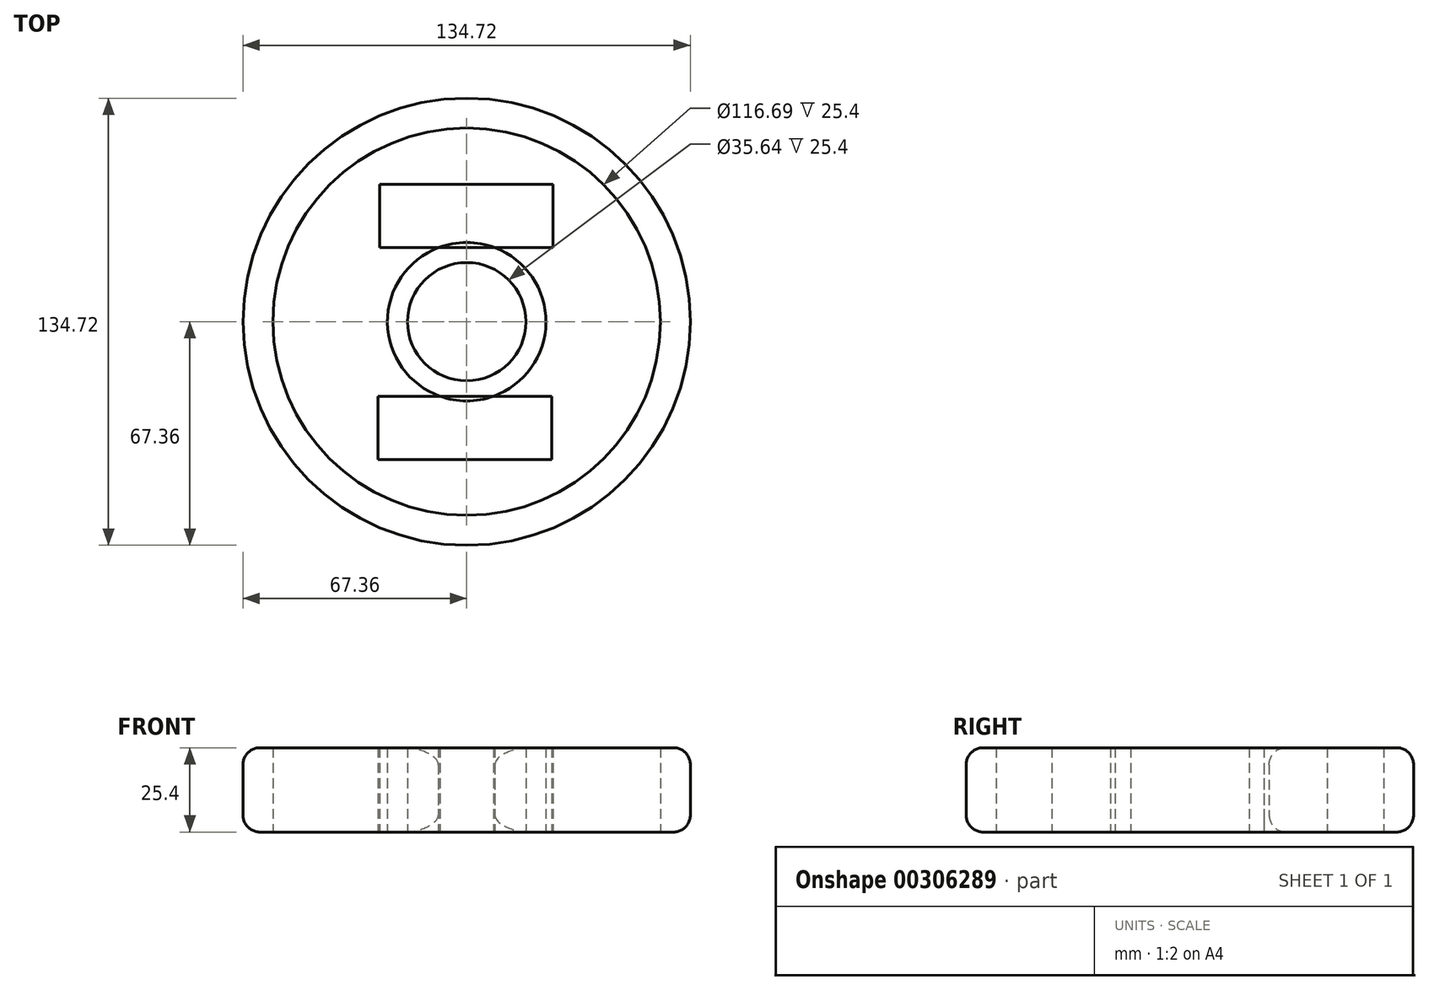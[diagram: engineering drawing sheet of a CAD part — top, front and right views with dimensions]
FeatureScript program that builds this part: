
annotation { "Feature Type Name" : "Feature", "Feature Type Description" : "" }
export const myFeature = defineFeature(function(context is Context, id is Id, definition is map)
    precondition{}
    {
        {
            var Q0;
            Q0=qCreatedBy(makeId("Top.planeOp"),FACE);
            var sketch = newSketch(context, id + "F0", { "sketchPlane" : qUnion([Q0])});
            skCircle(sketch, "E0", {"center": v(0, 0) * mm, "radius": 23.87 * mm});
            skCircle(sketch, "E1", {"center": v(0, 0) * mm, "radius": 17.82 * mm});
            skCircle(sketch, "E2", {"center": v(0, 0) * mm, "radius": 58.35 * mm});
            skLineSegment(sketch, "E3", {"start": v(-26.25, 22.3) * mm, "end": v(26.02, 22.3) * mm});
            skLineSegment(sketch, "E4", {"start": v(26.02, 22.3) * mm, "end": v(26.02, 41.35) * mm});
            skLineSegment(sketch, "E5", {"start": v(-26.25, 22.3) * mm, "end": v(-26.25, 41.35) * mm});
            skLineSegment(sketch, "E6", {"start": v(-26.25, 41.35) * mm, "end": v(26.02, 41.35) * mm});
            skLineSegment(sketch, "E7", {"start": v(-26.7, -41.53) * mm, "end": v(25.57, -41.53) * mm});
            skLineSegment(sketch, "E8", {"start": v(25.57, -41.53) * mm, "end": v(25.57, -22.48) * mm});
            skLineSegment(sketch, "E9", {"start": v(-26.7, -41.53) * mm, "end": v(-26.7, -22.48) * mm});
            skLineSegment(sketch, "E10", {"start": v(-26.7, -22.48) * mm, "end": v(25.57, -22.48) * mm});
            skCircle(sketch, "E11", {"center": v(0, 0) * mm, "radius": 67.36 * mm});
            skSolve(sketch);
        }
        {
            var Q0;
            Q0 = qSketchRegion(id + "F0", true);
            var Q1;
            Q1=makeQuery(id+"F0.imprint","IMPRINT",FACE,{"disambiguationData":[TD([[makeQuery(id+"F0.imprint","IMPRINT",EDGE,{"derivedFrom":sQuery(id+"F0.wireOp",EDGE,"E1")}),-1.0]])]});
            var Q2;
            {var subQ0=sQuery(id+"F0.wireOp",EDGE,"E4");Q2=makeQuery(id+"F0.imprint","IMPRINT",FACE,{"disambiguationData":[TD([[makeQuery(id+"F0.imprint","IMPRINT",EDGE,{"derivedFrom":subQ0}),1.0]])]});}
            var Q3;
            Q3=makeQuery(id+"F0.imprint","IMPRINT",FACE,{"disambiguationData":[TD([[makeQuery(id+"F0.imprint","IMPRINT",EDGE,{"derivedFrom":sQuery(id+"F0.wireOp",EDGE,"E7")}),1.0]])]});
            extrude(context, id + "F1", {"entities" : qUnion([Q0, Q1, Q2, Q3]), "depth" : 25.4 * mm});
        }
        {
            var Q0;
            {var subQ0=sQuery(id+"F0.wireOp",EDGE,"E0");Q0=makeQuery(id+"F1.opExtrude","CAP_EDGE",EDGE,{"disambiguationData":[OSD([subQ0]),TDD([makeQuery(id+"F0.imprint","IMPRINT",EDGE,{"disambiguationData":[TD([[makeQuery(id+"F0.imprint","INTERSECT",VERTEX,{"disambiguationData":[OD(1.0)],"derivedFrom":[subQ0,sQuery(id+"F0.wireOp",EDGE,"E3")]}),1.0]])],"derivedFrom":subQ0})])],"isStart":false});}
            var Q1;
            {var subQ0=sQuery(id+"F0.wireOp",EDGE,"E0");Q1=makeQuery(id+"F1.opExtrude","CAP_EDGE",EDGE,{"disambiguationData":[OSD([subQ0]),TDD([makeQuery(id+"F0.imprint","IMPRINT",EDGE,{"disambiguationData":[TD([[makeQuery(id+"F0.imprint","INTERSECT",VERTEX,{"disambiguationData":[OD(0.0)],"derivedFrom":[subQ0,sQuery(id+"F0.wireOp",EDGE,"E3")]}),-1.0]])],"derivedFrom":subQ0})])],"isStart":false});}
            var Q2;
            Q2=makeQuery(id+"F1.opExtrude","CAP_EDGE",EDGE,{"disambiguationData":[OSD([sQuery(id+"F0.wireOp",EDGE,"E11")])],"isStart":false});
            var Q3;
            Q3=makeQuery(id+"F1.opExtrude","CAP_EDGE",EDGE,{"disambiguationData":[OSD([sQuery(id+"F0.wireOp",EDGE,"E11")])],"isStart":true});
            var Q4;
            {var subQ0=sQuery(id+"F0.wireOp",EDGE,"E0");Q4=makeQuery(id+"F1.opExtrude","CAP_EDGE",EDGE,{"disambiguationData":[OSD([subQ0]),TDD([makeQuery(id+"F0.imprint","IMPRINT",EDGE,{"disambiguationData":[TD([[makeQuery(id+"F0.imprint","INTERSECT",VERTEX,{"disambiguationData":[OD(0.0)],"derivedFrom":[subQ0,sQuery(id+"F0.wireOp",EDGE,"E3")]}),-1.0]])],"derivedFrom":subQ0})])],"isStart":true});}
            var Q5;
            {var subQ0=sQuery(id+"F0.wireOp",EDGE,"E0");Q5=makeQuery(id+"F1.opExtrude","CAP_EDGE",EDGE,{"disambiguationData":[OSD([subQ0]),TDD([makeQuery(id+"F0.imprint","IMPRINT",EDGE,{"disambiguationData":[TD([[makeQuery(id+"F0.imprint","INTERSECT",VERTEX,{"disambiguationData":[OD(1.0)],"derivedFrom":[subQ0,sQuery(id+"F0.wireOp",EDGE,"E3")]}),1.0]])],"derivedFrom":subQ0})])],"isStart":true});}
            fillet(context, id + "F2", {"entities" : qUnion([Q0, Q1, Q2, Q3, Q4, Q5]), "radius" : 5.08 * mm, "tangentPropagation" : true, "allowEdgeOverflow" : false});
        }
    });
